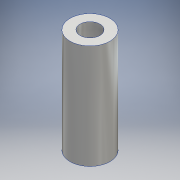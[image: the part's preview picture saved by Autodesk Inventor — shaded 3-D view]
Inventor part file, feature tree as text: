
AUTODESK INVENTOR PART (.ipt)
format: ipt  version: 2016 (Build 200138000, 138)  size: 109,056 bytes
history: native  units: mm
features: sketch x2, extrude x2, hole x2, other x1
ambient origin geometry x8: Origin, YZ Plane, XZ Plane, XY Plane, X Axis, Y Axis, Z Axis, Center Point
bodies: Body1 (feature_tree)
feature tree (7):
  other  "ソリッド1"
  sketch  "スケッチ1"
  extrude  "押し出し1"  Depth=8.0mm
  sketch  "スケッチ2"
  extrude  "押し出し2"  Depth=4.001mm
  hole  "穴1"  [1 undecoded]
  hole  "穴2"  [1 undecoded]
note: 2 required parameter values undecoded (feature->parameter linkage not recoverable at this tier; creation-order binding heuristic only, values carry confidence <= 0.55)
